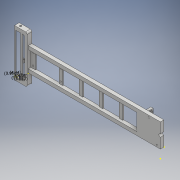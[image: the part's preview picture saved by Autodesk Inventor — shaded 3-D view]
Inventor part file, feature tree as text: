
AUTODESK INVENTOR PART (.ipt)
format: ipt  version: 2018 (Build 220112000, 112)  size: 545,280 bytes
history: native  units: mm
features: sketch x21, extrude x14, fillet x6, hole x4
ambient origin geometry x8: Origin, YZ Plane, XZ Plane, XY Plane, X Axis, Y Axis, Z Axis, Center Point
bodies: Solid1 (feature_tree)
feature tree (45):
  extrude  "Extrusion1"  Depth=50.0mm
  hole  "Hole1"  [1 undecoded]
  hole  "Hole2"  [1 undecoded]
  extrude  "Extrusion2"  Depth=25.0mm
  extrude  "Extrusion3"  Depth=25.0mm
  extrude  "Extrusion4"  Depth=5.0mm
  sketch  "Sketch7"  dims[d25=10.0mm d26=5.0mm]
  extrude  "Extrusion5"  Depth=5.0mm
  extrude  "Extrusion6"  Depth=35.0mm
  extrude  "Extrusion7"  Depth=35.0mm
  extrude  "Extrusion8"  Depth=35.0mm
  extrude  "Extrusion9"  Depth=2.0mm TaperAngle=0.0deg
  extrude  "Extrusion10"  Depth=7.5mm TaperAngle=0.0deg
  extrude  "Extrusion11"  Depth=10.0mm
  extrude  "Extrusion12"  Depth=7.5mm
  fillet  "Fillet1"  Radius=7.5mm
  fillet  "Fillet2"  Radius=25.0mm
  fillet  "Fillet3"  Radius=3.0mm
  fillet  "Fillet4"  Radius=3.2mm
  fillet  "Fillet5"  Radius=2.1mm
  fillet  "Fillet6"  Radius=5.5mm
  extrude  "Extrusion13"  Depth=92.5mm TaperAngle=0.0deg
  sketch  "Sketch17"  dims[d58=4.25mm d59=241.0mm d60=0.0mm]
  hole  "Hole3"  [1 undecoded]
  hole  "Hole4"  [1 undecoded]
  extrude  "Extrusion14"  Depth=5.0mm
  sketch  "Sketch21"  dims[d66=30.0mm d67=6.35mm d68=3.8mm d69=0.0mm d70=2.5mm d71=14.55mm d72=0.0mm d73=14.55mm d74=0.0mm d75=1.0mm d76=1.0mm d77=3.25mm d78=3.25mm d79=3.25mm d80=3.25mm d81=35.0mm d82=10.0mm d83=2.0mm d84=0.0mm d85=3.6mm d86=3.6mm d87=3.3mm d88=6.0mm d89=4.0mm d90=2.0mm d91=90.0deg d92=15.0mm d93=20.594885mm d94=3.3mm d95=6.0mm d96=4.0mm d97=2.0mm d98=90.0deg d99=15.0mm d100=20.594885mm d101=6.0mm d102=20.0mm d103=0.0mm d104=3.3mm d105=5.5mm d106=3.2mm d107=4.25mm d108=4.44mm d109=5.0mm d110=0.96mm]
  sketch  "Sketch1"  dims[d0=50.0mm d1=50.0mm]
  sketch  "Sketch2"  dims[d2=240.0mm d3=7.5mm]
  sketch  "Sketch3"  dims[d4=7.5mm d5=7.5mm d6=0.0mm]
  sketch  "Sketch4"  dims[d7=6.35mm d8=6.0mm d9=4.0mm d10=2.0mm d11=90.0deg d12=8.0mm d13=20.594885mm d14=25.0mm]
  sketch  "Sketch5"  dims[d15=3.3mm d16=6.0mm d17=4.0mm d18=2.0mm d19=90.0deg d20=8.0mm d21=20.594885mm d22=25.0mm]
  sketch  "Sketch6"  dims[d23=180.0deg d24=5.0mm]
  sketch  "Sketch8"  dims[d27=17.5mm d28=0.0mm d30=35.0mm]
  sketch  "Sketch9"  dims[d31=35.0mm d32=35.0mm]
  sketch  "Sketch10"  dims[d33=35.0mm d34=35.0mm]
  sketch  "Sketch11"  dims[d35=35.0mm d36=2.0mm d37=0.0mm]
  sketch  "Sketch12"  dims[d38=10.0mm d39=7.5mm d40=0.0mm]
  sketch  "Sketch13"  dims[d41=100.0mm d42=10.0mm]
  sketch  "Sketch14"  dims[d43=7.5mm d44=0.0mm d45=7.5mm d46=7.5mm d47=25.0mm d48=0.0mm d49=3.0mm d50=3.2mm d51=2.1mm d52=5.5mm]
  sketch  "Sketch15"  dims[d53=3.3mm d54=92.5mm d55=0.0mm]
  sketch  "Sketch16"  dims[d56=5.5mm d57=3.3mm]
  sketch  "Sketch18"  dims[d61=4.44mm d62=5.0mm]
  sketch  "Sketch19"  dims[d63=2.5mm]
  sketch  "Sketch20"  dims[d64=91.25mm d65=0.0mm]
note: 4 required parameter values undecoded (feature->parameter linkage not recoverable at this tier; creation-order binding heuristic only, values carry confidence <= 0.55)
